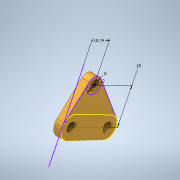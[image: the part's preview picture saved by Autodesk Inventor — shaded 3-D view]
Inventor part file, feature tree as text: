
AUTODESK INVENTOR PART (.ipt)
format: ipt  version: 2020 (Build 240168000, 168)  size: 153,600 bytes
history: native  units: in
note: dims shown in document units (in); Inventor stores cm internally (conversion verified against a paired STEP export)
features: extrude x3, sketch x3, projected_geometry x1
ambient origin geometry x8: Origin, YZ Plane, XZ Plane, XY Plane, X Axis, Y Axis, Z Axis, Center Point
bodies: Solid1 (feature_tree)
feature tree (7):
  extrude  "Extrusion1"  Depth=0.4523in
  extrude  "Extrusion2"  Depth=0.2118in
  extrude  "Extrusion3"  Depth=0.1575in TaperAngle=0.0deg
  sketch  "Sketch1"  dims[d0=0.2008in d1=0.2008in d3=0.4523in]
  sketch  "Sketch2"  dims[d4=0.2118in d5=0.8586in]
  projected_geometry  "Projected Loop1"
  sketch  "Sketch3"  dims[d6=0.8656in d7=0.1575in d8=0.0in d11=0.0787in d12=0.315in d13=0.1575in d14=0.0in d15=0.1969in d16=0.0787in d17=0.0in d20=0.7087in d21=0.4228in]
